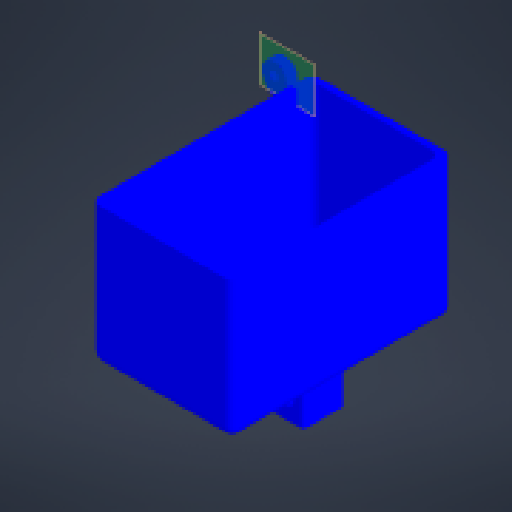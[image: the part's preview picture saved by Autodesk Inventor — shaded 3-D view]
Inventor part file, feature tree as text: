
AUTODESK INVENTOR PART (.ipt)
format: ipt  version: 2024 (Build 280153000, 153)  size: 402,432 bytes
history: native  units: mm
features: other x13, sketch x7, extrude x7, fillet x5, reference x5, projected_geometry x2, mirror x1
ambient origin geometry x8: Origin, YZ Plane, XZ Plane, XY Plane, X Axis, Y Axis, Z Axis, Center Point
bodies: Body1 (feature_tree)
feature tree (40):
  other  "Твердое тело1"
  sketch  "Эскиз1"
  other  "РабПлоскость1"
  extrude  "Выдавливание1"  Depth=15.0mm
  extrude  "Выдавливание2"  Depth=15.0mm
  extrude  "Выдавливание3"  Depth=3.0mm
  extrude  "Выдавливание4"  Depth=10.0mm TaperAngle=0.0deg
  fillet  "Сопряжение3"  Radius=3.0mm
  fillet  "Сопряжение5"  Radius=3.0mm
  fillet  "Сопряжение6"  Radius=3.0mm
  fillet  "Сопряжение8"  Radius=17.0mm
  fillet  "Сопряжение9"  Radius=3.0mm
  extrude  "Выдавливание13"  Depth=3.0mm
  other  "РабПлоскость11"
  extrude  "Выдавливание16"  Depth=3.0mm
  other  "РабПлоскость12"
  mirror  "Зеркальное отражение6"
  other  "РабПлоскость13"
  extrude  "Выдавливание17"  Depth=63.25mm TaperAngle=0.0deg
  reference  "Ссылка1"
  reference  "Ссылка2"
  reference  "Ссылка3"
  reference  "Ссылка4"
  sketch  "Эскиз2"
  sketch  "Эскиз3"
  sketch  "Эскиз4"
  reference  "Ссылка21"
  projected_geometry  "Спроецированная петля1"
  projected_geometry  "Спроецированная петля2"
  sketch  "Эскиз19"
  sketch  "Эскиз24"
  sketch  "Эскиз26"
  parser-record x2  (decoder bookkeeping rows leaked as tree rows — omitted from the tree; the rows remain in map.json)
  other  "main_assembly.iam"
  other  "base_assembly:1"
  other  "section:4"
  other  "main axis:1"
  other  "back_box_asembly.iam"
  other  "back_box_cup:1"
note: 2 file-system paths scrubbed to <path> (originals preserved in map.json)
